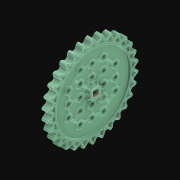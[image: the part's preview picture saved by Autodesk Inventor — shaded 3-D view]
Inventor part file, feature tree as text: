
AUTODESK INVENTOR PART (.ipt)
format: ipt  version: 2021 (Build 250183000, 183)  size: 7,085,056 bytes
history: native  units: in
note: dims shown in document units (in); Inventor stores cm internally (conversion verified against a paired STEP export)
features: sketch x1, other x1, fillet x1, extrude x1
ambient origin geometry x8: Origin, YZ Plane, XZ Plane, XY Plane, X Axis, Y Axis, Z Axis, Center Point
bodies: Solid1 (feature_tree)
feature tree (4):
  sketch  "Sketch1"
  other  "Srf1"
  fillet  "Fillet12"  Radius=0.3937in
  extrude  "ExtrusionSrf1"  [1 undecoded]
note: 1 required parameter value undecoded (feature->parameter linkage not recoverable at this tier; creation-order binding heuristic only, values carry confidence <= 0.55)
